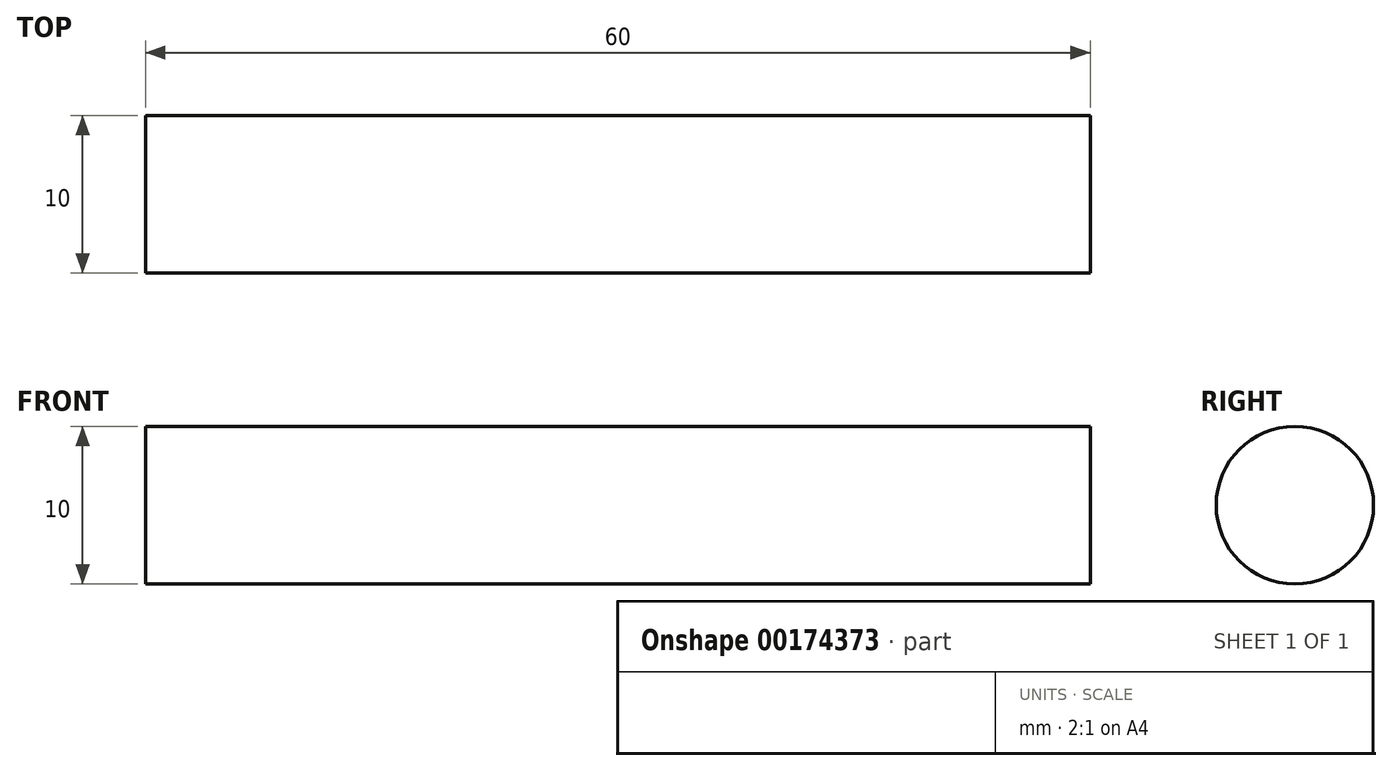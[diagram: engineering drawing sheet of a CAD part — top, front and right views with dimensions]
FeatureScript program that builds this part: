
annotation { "Feature Type Name" : "Feature", "Feature Type Description" : "" }
export const myFeature = defineFeature(function(context is Context, id is Id, definition is map)
    precondition{}
    {
        {
            var Q0;
            Q0=qCreatedBy(makeId("Front.planeOp"),FACE);
            var sketch = newSketch(context, id + "F0", { "sketchPlane" : qUnion([Q0])});
            skLineSegment(sketch, "E0.bottom", {"start": v(-30, 0) * mm, "end": v(30, 0) * mm});
            skLineSegment(sketch, "E0.top", {"start": v(-30, 5) * mm, "end": v(30, 5) * mm});
            skLineSegment(sketch, "E0.left", {"start": v(-30, 0) * mm, "end": v(-30, 5) * mm});
            skLineSegment(sketch, "E0.right", {"start": v(30, 0) * mm, "end": v(30, 5) * mm});
            skSolve(sketch);
        }
        {
            var Q0;
            Q0=makeQuery(id+"F0.imprint","IMPRINT",FACE,{"disambiguationData":[TD([[makeQuery(id+"F0.imprint","IMPRINT",EDGE,{"derivedFrom":sQuery(id+"F0.wireOp",EDGE,"E0.bottom")}),1.0]])]});
            var Q1;
            Q1=sQuery(id+"F0.wireOp",EDGE,"E0.right");
            var Q2;
            Q2=sQuery(id+"F0.wireOp",EDGE,"E0.left");
            var Q3;
            Q3=sQuery(id+"F0.wireOp",EDGE,"E0.top");
            var Q4;
            Q4=sQuery(id+"F0.wireOp",EDGE,"E0.bottom");
            var Q5;
            Q5=sQuery(id+"F0.wireOp",EDGE,"E0.bottom");
            revolve(context, id + "F1", {"entities" : qUnion([Q0]), "surfaceEntities" : qUnion([Q1, Q2, Q3, Q4]), "axis" : qUnion([Q5]), "revolveType" : RevolveType.FULL});
        }
    });
